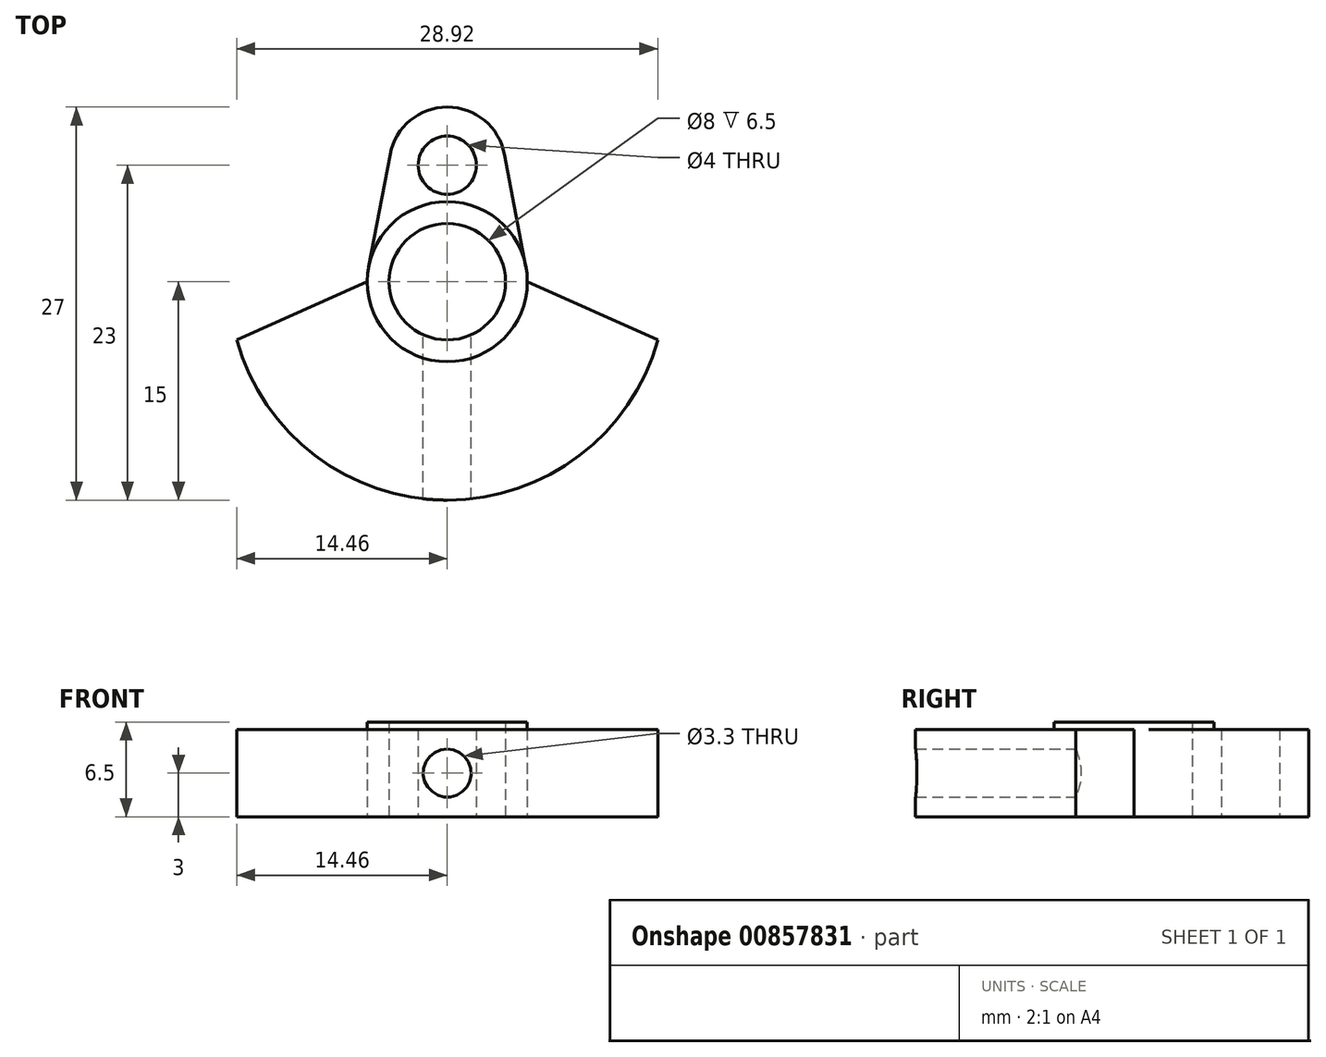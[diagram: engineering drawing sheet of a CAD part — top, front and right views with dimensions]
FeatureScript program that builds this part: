
annotation { "Feature Type Name" : "Feature", "Feature Type Description" : "" }
export const myFeature = defineFeature(function(context is Context, id is Id, definition is map)
    precondition{}
    {
        {
            var Q0;
            Q0=qCreatedBy(makeId("Top.planeOp"),FACE);
            var sketch = newSketch(context, id + "F0", { "sketchPlane" : qUnion([Q0])});
            skArc(sketch, "E0", {"start": v(-14.46, -4) * mm, "mid": v(0, -15) * mm, "end": v(14.46, -4) * mm});
            skArc(sketch, "E1", {"start": v(5.5, 0) * mm, "mid": v(5.48, 0.52) * mm, "end": v(5.4, 1.03) * mm});
            skLineSegment(sketch, "E2", {"start": v(-5.5, 0) * mm, "end": v(-14.46, -4) * mm});
            skLineSegment(sketch, "E3", {"start": v(5.5, 0) * mm, "end": v(14.46, -4) * mm});
            skArc(sketch, "E4", {"start": v(3.93, 8.75) * mm, "mid": v(0, 12) * mm, "end": v(-3.93, 8.75) * mm});
            skLineSegment(sketch, "E5", {"start": v(-5.4, 1.03) * mm, "end": v(-3.93, 8.75) * mm});
            skLineSegment(sketch, "E6", {"start": v(3.93, 8.75) * mm, "end": v(5.4, 1.03) * mm});
            skArc(sketch, "E7.trimOffspring", {"start": v(-5.4, 1.03) * mm, "mid": v(-5.48, 0.52) * mm, "end": v(-5.5, 0) * mm});
            skCircle(sketch, "E8", {"center": v(0, 0) * mm, "radius": 4 * mm});
            skCircle(sketch, "E9", {"center": v(0, 8) * mm, "radius": 2 * mm});
            skSolve(sketch);
        }
        {
            var Q0;
            Q0=makeQuery(id+"F0.imprint","IMPRINT",FACE,{"disambiguationData":[TD([[makeQuery(id+"F0.imprint","IMPRINT",EDGE,{"derivedFrom":sQuery(id+"F0.wireOp",EDGE,"E0")}),1.0]])]});
            extrude(context, id + "F1", {"entities" : qUnion([Q0]), "depth" : 6 * mm, "offsetDistance" : 25 * mm});
        }
        {
            var Q0;
            Q0=makeQuery(id+"F1.opExtrude","CAP_FACE",FACE,{"disambiguationData":[OSD([sQuery(id+"F0.wireOp",EDGE,"E0"),sQuery(id+"F0.wireOp",EDGE,"E1"),sQuery(id+"F0.wireOp",EDGE,"E2"),sQuery(id+"F0.wireOp",EDGE,"E3"),sQuery(id+"F0.wireOp",EDGE,"E4"),sQuery(id+"F0.wireOp",EDGE,"E5"),sQuery(id+"F0.wireOp",EDGE,"E6"),sQuery(id+"F0.wireOp",EDGE,"E7.trimOffspring"),sQuery(id+"F0.wireOp",EDGE,"E8"),sQuery(id+"F0.wireOp",EDGE,"E9")])],"isStart":false});
            var sketch = newSketch(context, id + "F2", { "sketchPlane" : qUnion([Q0])});
            skCircle(sketch, "E10", {"center": v(0, 0) * mm, "radius": 4 * mm});
            skCircle(sketch, "E11", {"center": v(0, 0) * mm, "radius": 5.5 * mm});
            skSolve(sketch);
        }
        {
            var Q0;
            Q0=makeQuery(id+"F2.imprint","IMPRINT",FACE,{"disambiguationData":[TD([[makeQuery(id+"F2.imprint","IMPRINT",EDGE,{"derivedFrom":sQuery(id+"F2.wireOp",EDGE,"E10")}),-1.0]])]});
            extrude(context, id + "F3", {"entities" : qUnion([Q0]), "operationType" : NewBodyOperationType.ADD, "depth" : 0.5 * mm, "offsetDistance" : 25 * mm});
        }
        {
            var Q0;
            Q0=qCreatedBy(makeId("Front.planeOp"),FACE);
            var sketch = newSketch(context, id + "F4", { "sketchPlane" : qUnion([Q0])});
            skPoint(sketch, "E12", {"position": v(0, 3) * mm});
            skSolve(sketch);
        }
        {
            var Q0;
            Q0=sQuery(id+"F4.wireOp",VERTEX,"E12");
            var Q1;
            Q1=makeQuery(id+"F1.opExtrude","SWEPT_BODY",BODY,{"disambiguationData":[OSD([sQuery(id+"F0.wireOp",EDGE,"E0"),sQuery(id+"F0.wireOp",EDGE,"E1"),sQuery(id+"F0.wireOp",EDGE,"E2"),sQuery(id+"F0.wireOp",EDGE,"E3"),sQuery(id+"F0.wireOp",EDGE,"E4"),sQuery(id+"F0.wireOp",EDGE,"E5"),sQuery(id+"F0.wireOp",EDGE,"E6"),sQuery(id+"F0.wireOp",EDGE,"E7.trimOffspring"),sQuery(id+"F0.wireOp",EDGE,"E8"),sQuery(id+"F0.wireOp",EDGE,"E9")])]});
            hole(context, id + "F5", {"style" : HoleStyle.SIMPLE, "endStyle" : HoleEndStyle.THROUGH, "oppositeDirection" : true, "holeDiameter" : 3.3 * mm, "majorDiameter" : 4 * mm, "isTappedThrough" : true, "tappedDepth" : 6 * mm, "tapClearance" : 3, "locations" : qUnion([Q0]), "scope" : qUnion([Q1])});
        }
    });
